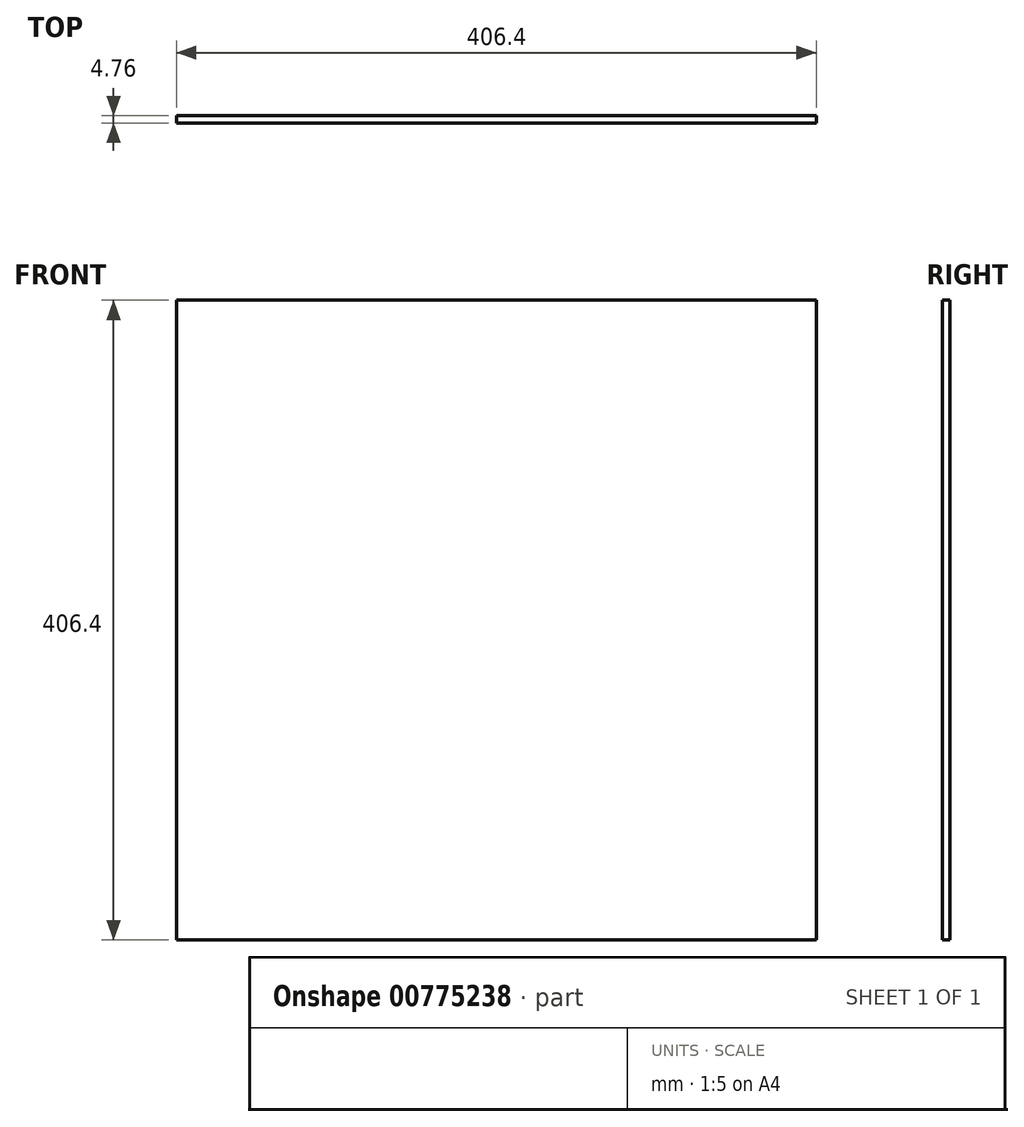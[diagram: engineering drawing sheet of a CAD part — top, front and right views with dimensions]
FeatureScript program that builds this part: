
annotation { "Feature Type Name" : "Feature", "Feature Type Description" : "" }
export const myFeature = defineFeature(function(context is Context, id is Id, definition is map)
    precondition{}
    {
        {
            var Q0;
            Q0=qCreatedBy(makeId("Front.planeOp"),FACE);
            var sketch = newSketch(context, id + "F0", { "sketchPlane" : qUnion([Q0])});
            skLineSegment(sketch, "E0.bottom", {"start": v(203.2, 203.2) * mm, "end": v(-203.2, 203.2) * mm});
            skLineSegment(sketch, "E0.top", {"start": v(203.2, -203.2) * mm, "end": v(-203.2, -203.2) * mm});
            skLineSegment(sketch, "E0.left", {"start": v(203.2, 203.2) * mm, "end": v(203.2, -203.2) * mm});
            skLineSegment(sketch, "E0.right", {"start": v(-203.2, 203.2) * mm, "end": v(-203.2, -203.2) * mm});
            skPoint(sketch, "E0.middle", {"position": v(0, 0) * mm});
            skSolve(sketch);
        }
        {
            var Q0;
            Q0=makeQuery(id+"F0.imprint","IMPRINT",FACE,{"disambiguationData":[TD([[makeQuery(id+"F0.imprint","IMPRINT",EDGE,{"derivedFrom":sQuery(id+"F0.wireOp",EDGE,"E0.bottom")}),1.0]])]});
            extrude(context, id + "F1", {"entities" : qUnion([Q0]), "endBound" : BoundingType.SYMMETRIC, "depth" : 4.76 * mm, "offsetDistance" : 25.4 * mm});
        }
    });
